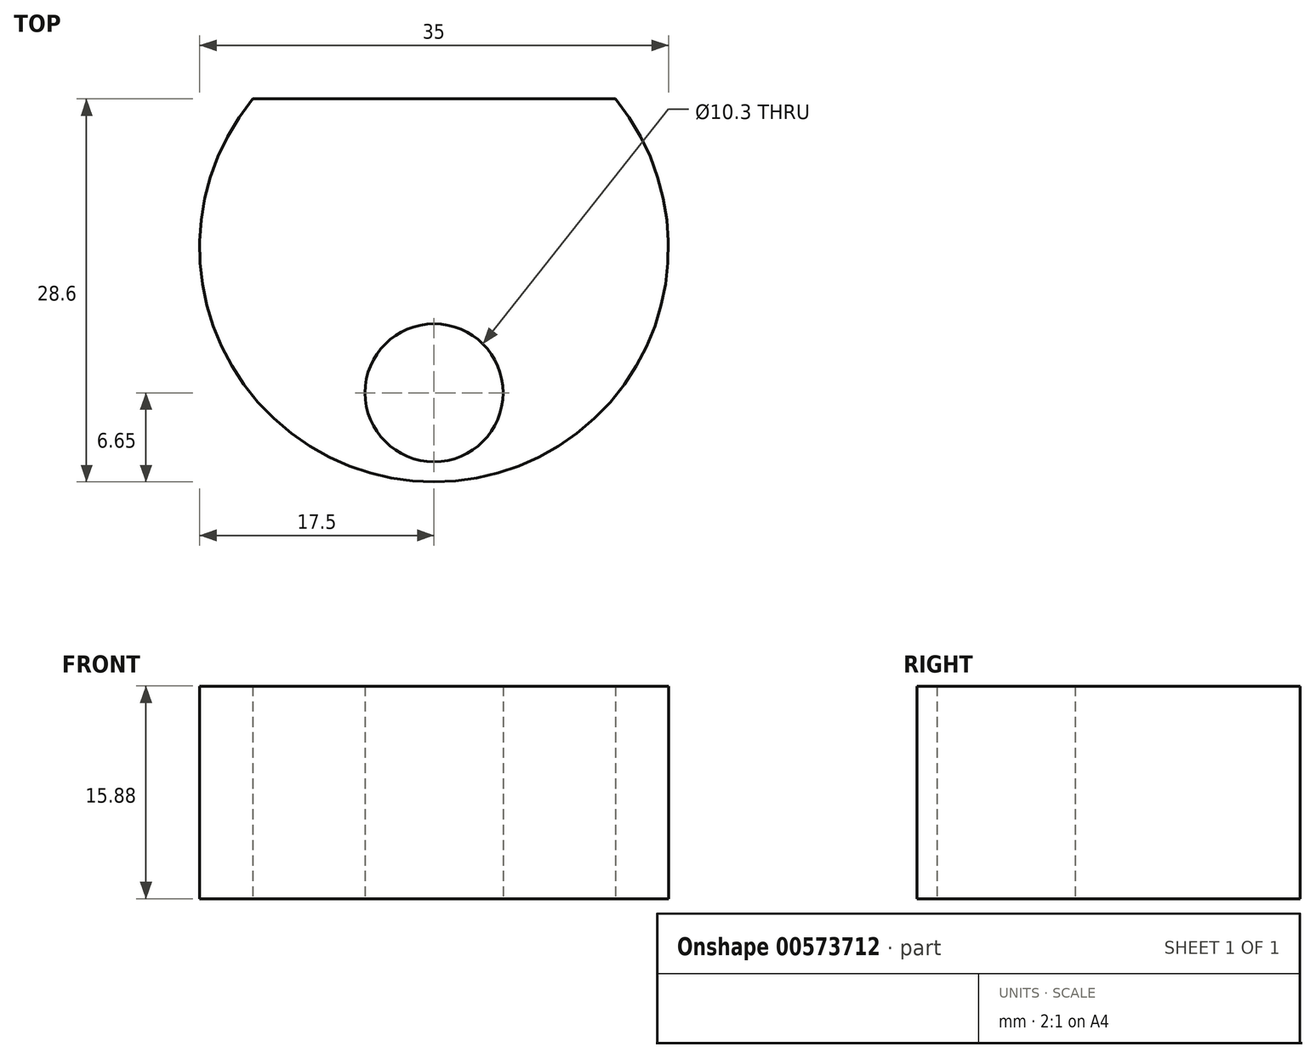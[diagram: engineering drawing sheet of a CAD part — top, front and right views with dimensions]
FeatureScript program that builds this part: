
annotation { "Feature Type Name" : "Feature", "Feature Type Description" : "" }
export const myFeature = defineFeature(function(context is Context, id is Id, definition is map)
    precondition{}
    {
        {
            var Q0;
            Q0=qCreatedBy(makeId("Top.planeOp"),FACE);
            var sketch = newSketch(context, id + "F0", { "sketchPlane" : qUnion([Q0])});
            skArc(sketch, "E0", {"start": v(-13.53, 11.1) * mm, "mid": v(0, -17.5) * mm, "end": v(13.53, 11.1) * mm});
            skCircle(sketch, "E1", {"center": v(0, -10.85) * mm, "radius": 5.15 * mm});
            skLineSegment(sketch, "E2", {"start": v(-13.53, 11.1) * mm, "end": v(13.53, 11.1) * mm});
            skSolve(sketch);
        }
        {
            var Q0;
            Q0 = qSketchRegion(id + "F0", true);
            extrude(context, id + "F1", {"entities" : qUnion([Q0]), "depth" : 15.88 * mm, "offsetDistance" : 25 * mm});
        }
    });
